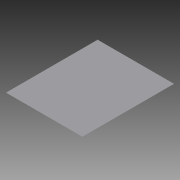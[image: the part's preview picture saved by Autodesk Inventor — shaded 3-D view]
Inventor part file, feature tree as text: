
AUTODESK INVENTOR PART (.ipt)
format: ipt  version: 2018.2 (Build 222227000, 227)  size: 78,848 bytes
history: native  units: mm
features: extrude x1, chamfer x1, sketch x1
ambient origin geometry x8: Origin, YZ Plane, XZ Plane, XY Plane, X Axis, Y Axis, Z Axis, Center Point
bodies: Volumenkörper1 (feature_tree)
feature tree (3):
  extrude  "Extrusion1"  Depth=20.0mm
  chamfer  "Fase1"  Distance=20.0mm
  sketch  "Skizze1"  dims[d0=500.0mm d1=600.0mm d2=20.0mm d3=0.0mm d4=20.0mm d5=2.0mm d6=45.0deg]
